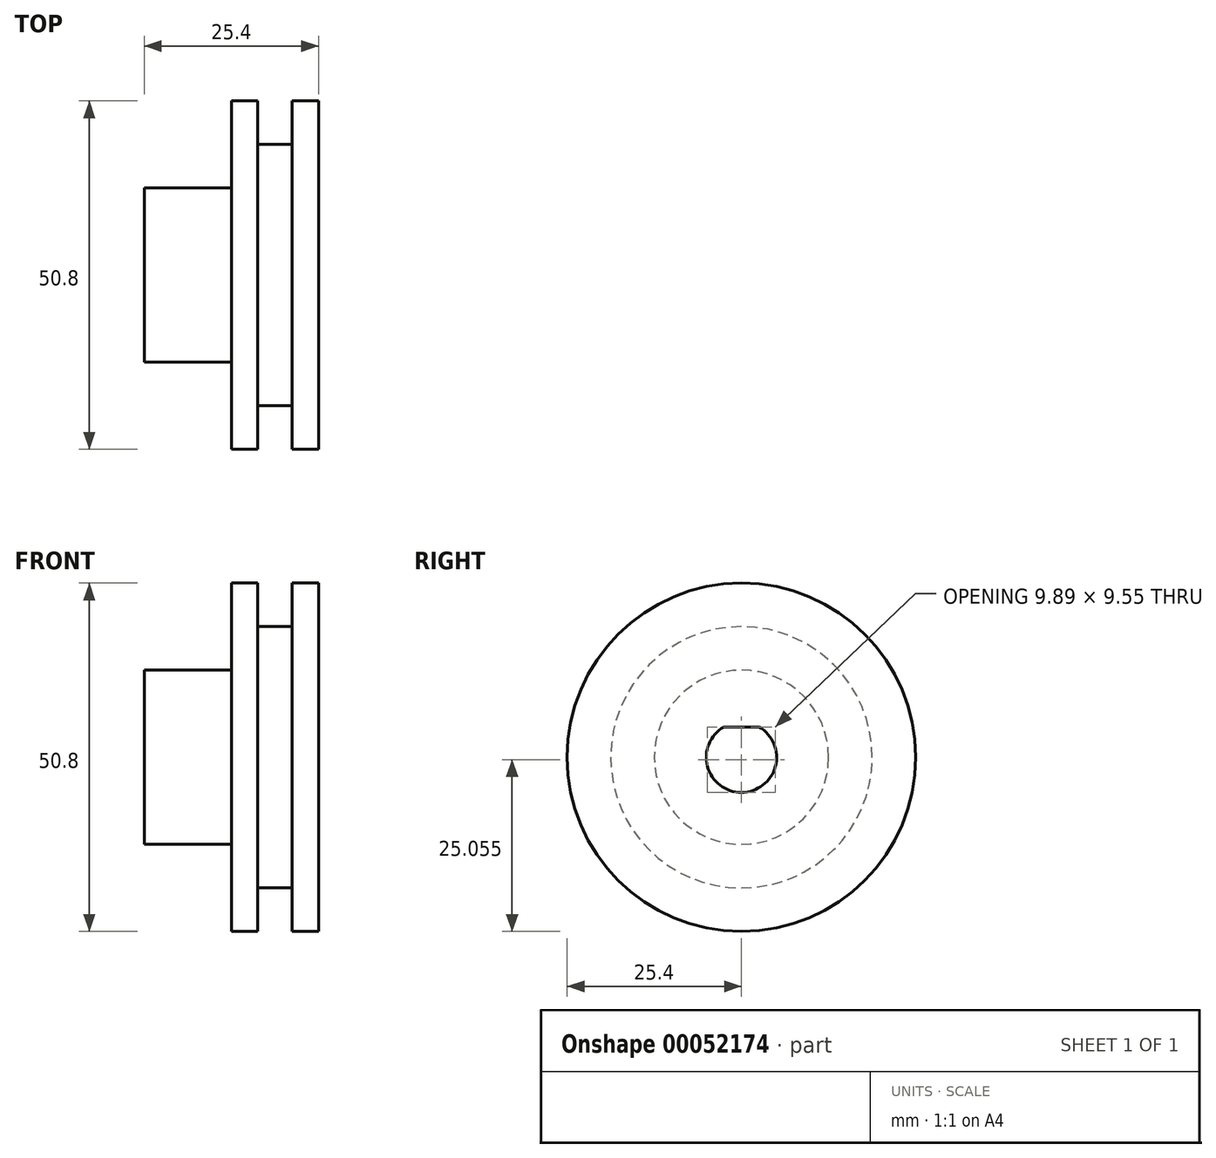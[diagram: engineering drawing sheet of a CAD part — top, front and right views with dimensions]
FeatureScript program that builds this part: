
annotation { "Feature Type Name" : "Feature", "Feature Type Description" : "" }
export const myFeature = defineFeature(function(context is Context, id is Id, definition is map)
    precondition{}
    {
        {
            var Q0;
            Q0=qCreatedBy(makeId("Right.planeOp"),FACE);
            var sketch = newSketch(context, id + "F0", { "sketchPlane" : qUnion([Q0])});
            skCircle(sketch, "E0", {"center": v(0, 0) * mm, "radius": 25.4 * mm});
            skSolve(sketch);
        }
        {
            var Q0;
            Q0=makeQuery(id+"F0.imprint","IMPRINT",FACE,{"disambiguationData":[TD([[makeQuery(id+"F0.imprint","IMPRINT",EDGE,{"derivedFrom":sQuery(id+"F0.wireOp",EDGE,"E0")}),1.0]])]});
            extrude(context, id + "F1", {"entities" : qUnion([Q0]), "endBound" : BoundingType.SYMMETRIC, "depth" : 12.7 * mm});
        }
        {
            var Q0;
            Q0=qCreatedBy(makeId("Right.planeOp"),FACE);
            var sketch = newSketch(context, id + "F2", { "sketchPlane" : qUnion([Q0])});
            skCircle(sketch, "E1", {"center": v(0, 0) * mm, "radius": 19.05 * mm});
            skCircle(sketch, "E2", {"center": v(0, 0) * mm, "radius": 25.4 * mm});
            skSolve(sketch);
        }
        {
            var Q0;
            Q0=qSketchRegion(id+"F2",true);
            extrude(context, id + "F3", {"entities" : qUnion([Q0]), "operationType" : NewBodyOperationType.REMOVE, "endBound" : BoundingType.SYMMETRIC, "oppositeDirection" : true, "depth" : 5.08 * mm});
        }
        {
            var Q0;
            Q0=makeQuery(id+"F1.opExtrude","CAP_FACE",FACE,{"disambiguationData":[OSD([sQuery(id+"F0.wireOp",EDGE,"E0")])],"isStart":false});
            var sketch = newSketch(context, id + "F4", { "sketchPlane" : qUnion([Q0])});
            skArc(sketch, "E3", {"start": v(-2.57, 4.43) * mm, "mid": v(0, -5.12) * mm, "end": v(2.57, 4.43) * mm});
            skLineSegment(sketch, "E4", {"start": v(-2.57, 4.43) * mm, "end": v(2.57, 4.43) * mm});
            skSolve(sketch);
        }
        {
            var Q0;
            Q0=makeQuery(id+"F1.opExtrude","CAP_FACE",FACE,{"disambiguationData":[OSD([sQuery(id+"F0.wireOp",EDGE,"E0")])],"isStart":true});
            var sketch = newSketch(context, id + "F5", { "sketchPlane" : qUnion([Q0])});
            skCircle(sketch, "E5", {"center": v(0, 0) * mm, "radius": 12.7 * mm});
            skSolve(sketch);
        }
        {
            var Q0;
            Q0=makeQuery(id+"F5.imprint","IMPRINT",FACE,{"disambiguationData":[TD([[makeQuery(id+"F5.imprint","IMPRINT",EDGE,{"derivedFrom":sQuery(id+"F5.wireOp",EDGE,"E5")}),1.0]])]});
            extrude(context, id + "F6", {"entities" : qUnion([Q0]), "operationType" : NewBodyOperationType.ADD, "depth" : 12.7 * mm});
        }
        {
            var Q0;
            Q0=makeQuery(id+"F4.imprint","IMPRINT",FACE,{"disambiguationData":[TD([[makeQuery(id+"F4.imprint","IMPRINT",EDGE,{"derivedFrom":sQuery(id+"F4.wireOp",EDGE,"E3")}),1.0]])]});
            extrude(context, id + "F7", {"entities" : qUnion([Q0]), "operationType" : NewBodyOperationType.REMOVE, "endBound" : BoundingType.THROUGH_ALL, "oppositeDirection" : true, "depth" : 25.4 * mm});
        }
    });
